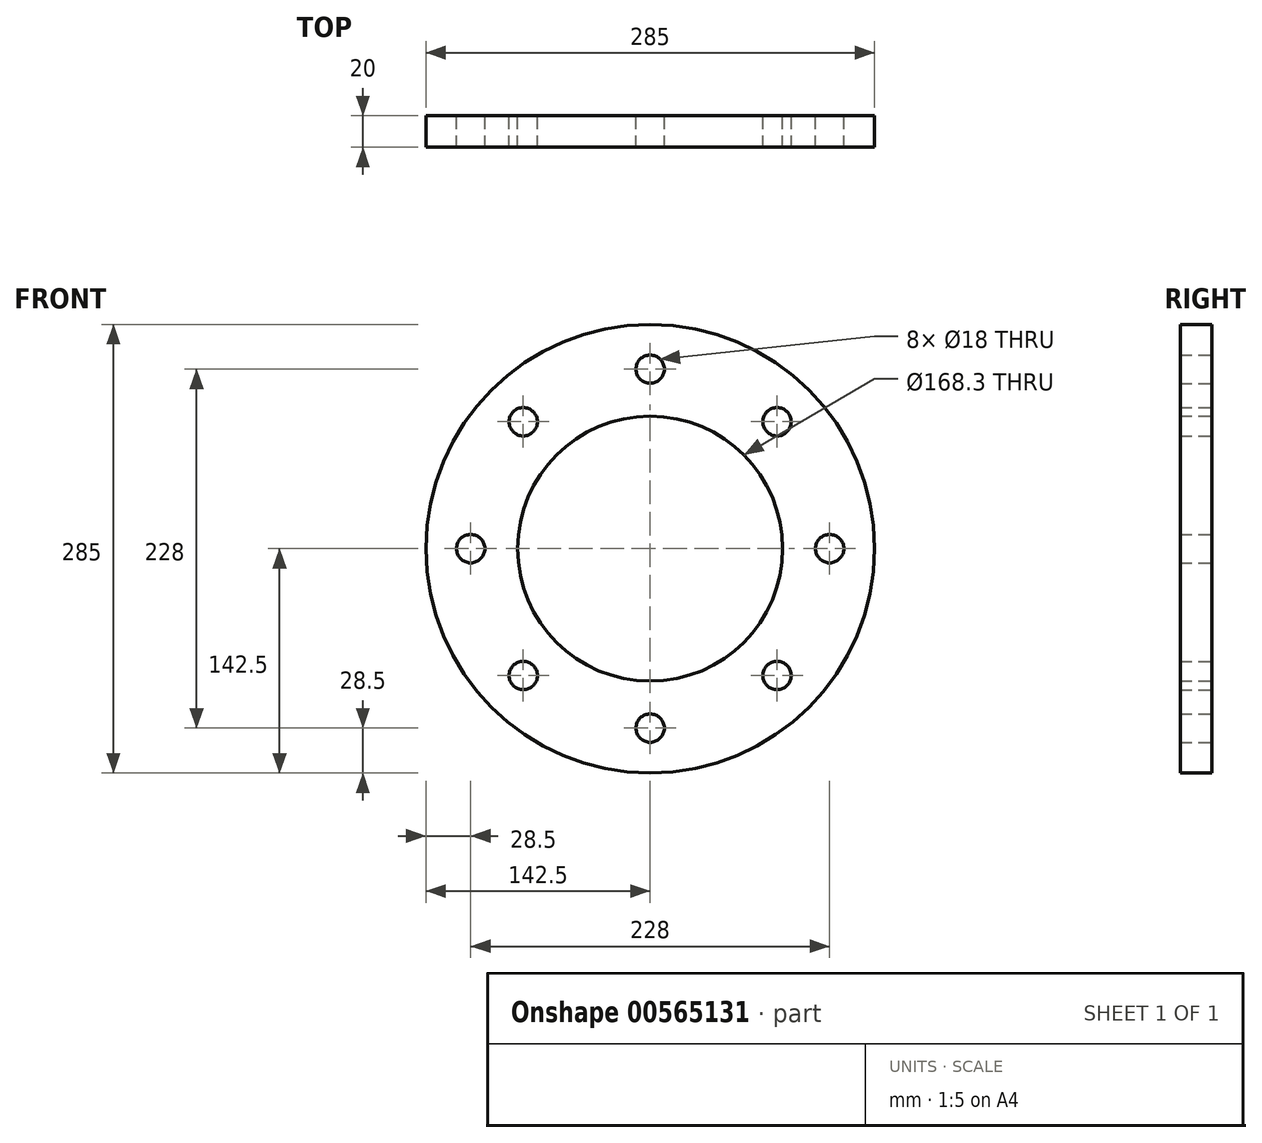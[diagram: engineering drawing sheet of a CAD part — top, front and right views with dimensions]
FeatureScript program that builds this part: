
annotation { "Feature Type Name" : "Feature", "Feature Type Description" : "" }
export const myFeature = defineFeature(function(context is Context, id is Id, definition is map)
    precondition{}
    {
        {
            var Q0;
            Q0=qCreatedBy(makeId("Front.planeOp"),FACE);
            var sketch = newSketch(context, id + "F0", { "sketchPlane" : qUnion([Q0])});
            skCircle(sketch, "E0", {"center": v(0, 0) * mm, "radius": 142.5 * mm});
            skCircle(sketch, "E1", {"center": v(0, 0) * mm, "radius": 84.15 * mm});
            skCircle(sketch, "E2", {"center": v(0, 0) * mm, "radius": 114 * mm, "construction": true});
            skLineSegment(sketch, "E3", {"start": v(0, 0) * mm, "end": v(100.76, 100.76) * mm, "construction": true});
            skLineSegment(sketch, "E4", {"start": v(0, 0) * mm, "end": v(100.76, -100.76) * mm, "construction": true});
            skLineSegment(sketch, "E5", {"start": v(0, 0) * mm, "end": v(-100.76, -100.76) * mm, "construction": true});
            skLineSegment(sketch, "E6", {"start": v(0, 0) * mm, "end": v(-100.76, 100.76) * mm, "construction": true});
            skCircle(sketch, "E7", {"center": v(0, 114) * mm, "radius": 9 * mm});
            skCircle(sketch, "E8", {"center": v(80.61, 80.61) * mm, "radius": 9 * mm});
            skCircle(sketch, "E9", {"center": v(114, 0) * mm, "radius": 9 * mm});
            skCircle(sketch, "E10", {"center": v(80.61, -80.61) * mm, "radius": 9 * mm});
            skCircle(sketch, "E11", {"center": v(0, -114) * mm, "radius": 9 * mm});
            skCircle(sketch, "E12", {"center": v(-80.61, -80.61) * mm, "radius": 9 * mm});
            skCircle(sketch, "E13", {"center": v(-114, 0) * mm, "radius": 9 * mm});
            skCircle(sketch, "E14", {"center": v(-80.61, 80.61) * mm, "radius": 9 * mm});
            skSolve(sketch);
        }
        {
            var Q0;
            Q0=makeQuery(id+"F0.imprint","IMPRINT",FACE,{"disambiguationData":[TD([[makeQuery(id+"F0.imprint","IMPRINT",EDGE,{"derivedFrom":sQuery(id+"F0.wireOp",EDGE,"E0")}),1.0]])]});
            extrude(context, id + "F1", {"entities" : qUnion([Q0]), "depth" : 20 * mm, "offsetDistance" : 25 * mm});
        }
    });
